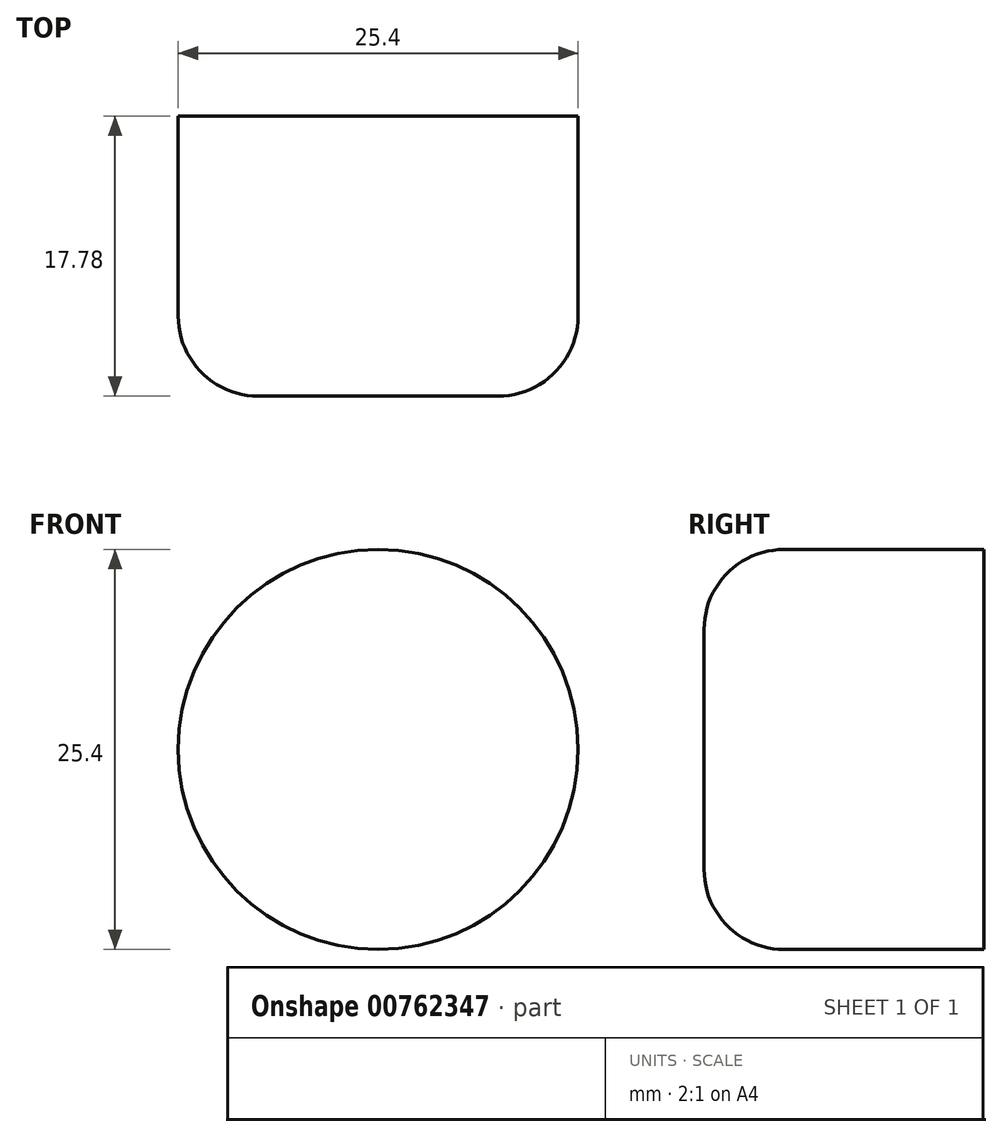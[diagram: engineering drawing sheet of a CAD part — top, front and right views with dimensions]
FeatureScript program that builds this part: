
annotation { "Feature Type Name" : "Feature", "Feature Type Description" : "" }
export const myFeature = defineFeature(function(context is Context, id is Id, definition is map)
    precondition{}
    {
        {
            var Q0;
            Q0=qCreatedBy(makeId("Front.planeOp"),FACE);
            var sketch = newSketch(context, id + "F0", { "sketchPlane" : qUnion([Q0])});
            skCircle(sketch, "E0", {"center": v(0, 0) * mm, "radius": 12.7 * mm});
            skSolve(sketch);
        }
        {
            var Q0;
            Q0=makeQuery(id+"F0.imprint","IMPRINT",FACE,{"disambiguationData":[TD([[makeQuery(id+"F0.imprint","IMPRINT",EDGE,{"derivedFrom":sQuery(id+"F0.wireOp",EDGE,"E0")}),1.0]])]});
            extrude(context, id + "F1", {"entities" : qUnion([Q0]), "depth" : 17.78 * mm, "offsetDistance" : 25.4 * mm});
        }
        {
            var Q0;
            Q0=makeQuery(id+"F1.opExtrude","CAP_FACE",FACE,{"disambiguationData":[OSD([sQuery(id+"F0.wireOp",EDGE,"E0")])],"isStart":false});
            fillet(context, id + "F2", {"entities" : qUnion([Q0]), "radius" : 5.08 * mm, "tangentPropagation" : true, "allowEdgeOverflow" : false});
        }
    });
